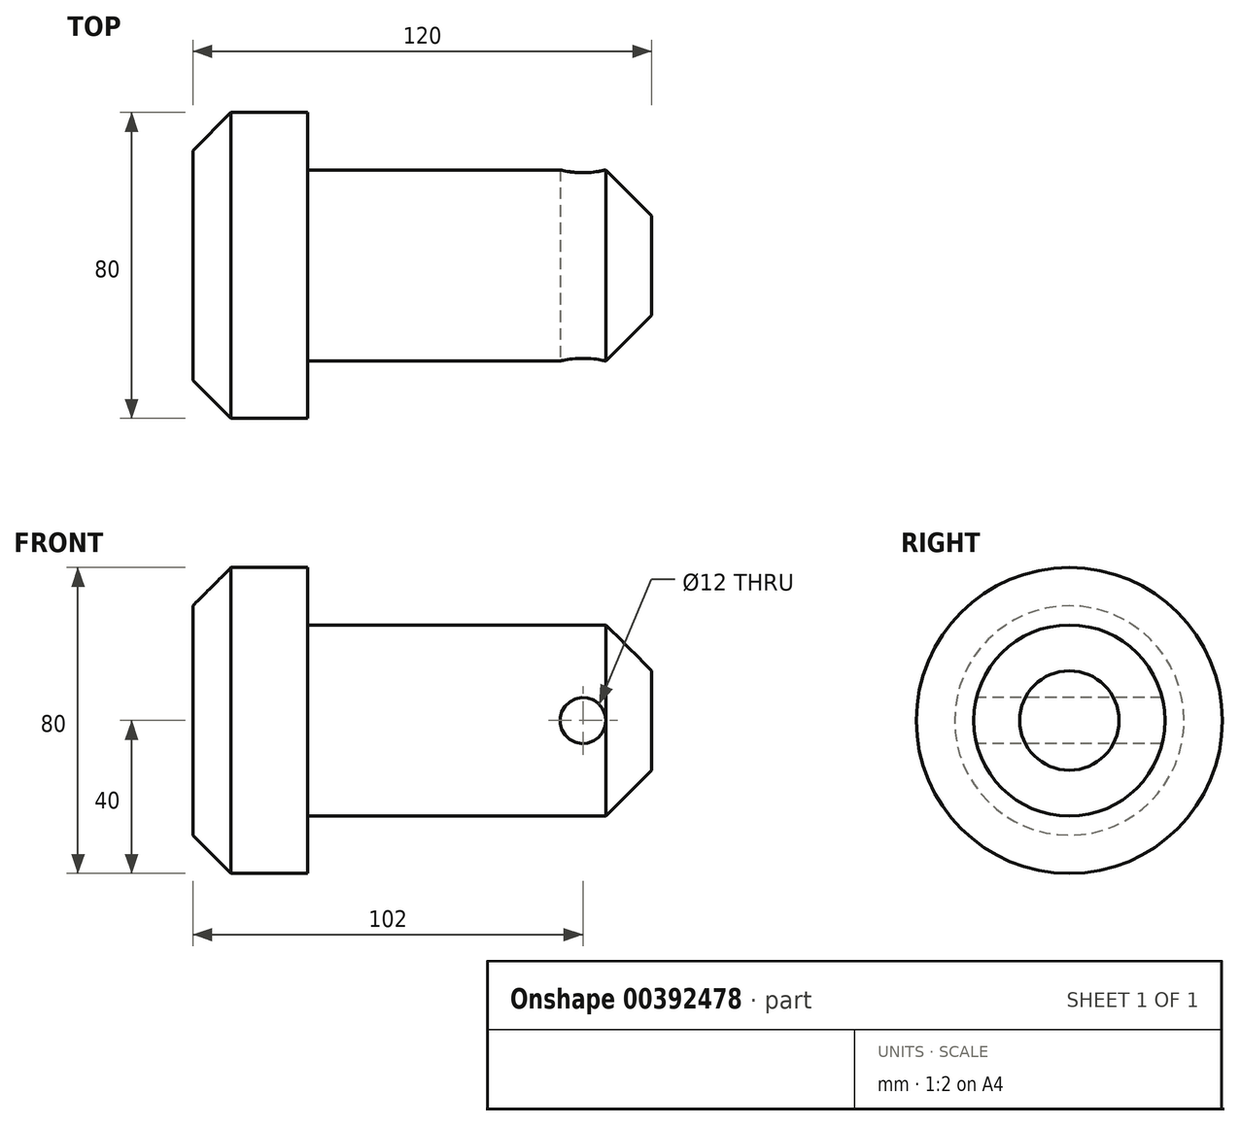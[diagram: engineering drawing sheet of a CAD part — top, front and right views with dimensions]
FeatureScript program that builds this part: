
annotation { "Feature Type Name" : "Feature", "Feature Type Description" : "" }
export const myFeature = defineFeature(function(context is Context, id is Id, definition is map)
    precondition{}
    {
        {
            var Q0;
            Q0=qCreatedBy(makeId("Front.planeOp"),FACE);
            var sketch = newSketch(context, id + "F0", { "sketchPlane" : qUnion([Q0])});
            skLineSegment(sketch, "E0.bottom", {"start": v(0, 0) * mm, "end": v(30, 0) * mm});
            skLineSegment(sketch, "E0.top", {"start": v(0, 40) * mm, "end": v(30, 40) * mm});
            skLineSegment(sketch, "E0.left", {"start": v(0, 0) * mm, "end": v(0, 40) * mm});
            skLineSegment(sketch, "E0.right", {"start": v(30, 0) * mm, "end": v(30, 40) * mm});
            skLineSegment(sketch, "E1.bottom", {"start": v(30, 0) * mm, "end": v(120, 0) * mm});
            skLineSegment(sketch, "E1.top", {"start": v(30, 25) * mm, "end": v(120, 25) * mm});
            skLineSegment(sketch, "E1.left", {"start": v(30, 0) * mm, "end": v(30, 25) * mm});
            skLineSegment(sketch, "E1.right", {"start": v(120, 0) * mm, "end": v(120, 25) * mm});
            skLineSegment(sketch, "E2", {"start": v(30, 0) * mm, "end": v(102, 0) * mm, "construction": true});
            skCircle(sketch, "E3", {"center": v(102, 0) * mm, "radius": 6 * mm});
            skLineSegment(sketch, "E4", {"start": v(108, 0) * mm, "end": v(120, 0) * mm, "construction": true});
            skSolve(sketch);
        }
        {
            var Q0;
            Q0 = qSketchRegion(id + "F0", true);
            var Q1;
            Q1=sQuery(id+"F0.wireOp",EDGE,"E1.bottom");
            revolve(context, id + "F1", {"entities" : qUnion([Q0]), "axis" : qUnion([Q1]), "revolveType" : RevolveType.FULL});
        }
        {
            var Q0;
            Q0=makeQuery(id+"F1.opRevolve","SWEPT_EDGE",EDGE,{"disambiguationData":[OSD([sQuery(id+"F0.wireOp",EDGE,"E0.top"),sQuery(id+"F0.wireOp",EDGE,"E0.left")])]});
            chamfer(context, id + "F2", {"entities" : qUnion([Q0]), "chamferType" : ChamferType.OFFSET_ANGLE, "width" : 10 * mm, "oppositeDirection" : false, "angle" : 45 * degree, "tangentPropagation" : true});
        }
        {
            var Q0;
            {var subQ0=sQuery(id+"F0.wireOp",EDGE,"E3");var subQ1=sQuery(id+"F0.wireOp",EDGE,"E1.bottom");var subQ2=makeQuery(id+"F0.imprint","INTERSECT",VERTEX,{"disambiguationData":[OD(0.0)],"derivedFrom":[subQ1,subQ0]});Q0=makeQuery(id+"F0.imprint","IMPRINT",FACE,{"disambiguationData":[TD([[makeQuery(id+"F0.imprint","IMPRINT",EDGE,{"disambiguationData":[TD([[subQ2,-1.0]])],"derivedFrom":subQ1}),1.0]])]});}
            var Q1;
            {var subQ0=sQuery(id+"F0.wireOp",EDGE,"E3");var subQ1=sQuery(id+"F0.wireOp",EDGE,"E1.bottom");var subQ2=makeQuery(id+"F0.imprint","INTERSECT",VERTEX,{"disambiguationData":[OD(0.0)],"derivedFrom":[subQ1,subQ0]});Q1=makeQuery(id+"F0.imprint","IMPRINT",FACE,{"disambiguationData":[TD([[makeQuery(id+"F0.imprint","IMPRINT",EDGE,{"disambiguationData":[TD([[subQ2,-1.0]])],"derivedFrom":subQ1}),-1.0]])]});}
            extrude(context, id + "F3", {"entities" : qUnion([Q0, Q1]), "operationType" : NewBodyOperationType.REMOVE, "endBound" : BoundingType.SYMMETRIC, "oppositeDirection" : true, "depth" : 50 * mm});
        }
        {
            var Q0;
            Q0=makeQuery(id+"F1.opRevolve","SWEPT_EDGE",EDGE,{"disambiguationData":[OSD([sQuery(id+"F0.wireOp",EDGE,"E1.top"),sQuery(id+"F0.wireOp",EDGE,"E1.right")])]});
            chamfer(context, id + "F4", {"entities" : qUnion([Q0]), "chamferType" : ChamferType.OFFSET_ANGLE, "width" : 12 * mm, "oppositeDirection" : false, "angle" : 45 * degree, "tangentPropagation" : true});
        }
    });
